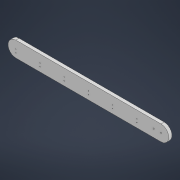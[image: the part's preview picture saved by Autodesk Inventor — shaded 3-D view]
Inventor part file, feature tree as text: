
AUTODESK INVENTOR PART (.ipt)
format: ipt  version: 2021 (Build 250183000, 183)  size: 128,000 bytes
history: native  units: mm
features: sketch x5, hole x3, extrude x2, plane x1, mirror x1
ambient origin geometry x8: Origin, YZ Plane, XZ Plane, XY Plane, X Axis, Y Axis, Z Axis, Center Point
bodies: Solid1 (feature_tree)
feature tree (12):
  extrude  "Extrusion1"  Depth=12.0mm
  hole  "Hole1"  [1 undecoded]
  hole  "Hole2"  [1 undecoded]
  hole  "Hole3"  [1 undecoded]
  plane  "Work Plane1"
  mirror  "Mirror1"
  extrude  "Extrusion2"  Depth=5.0mm
  sketch  "Sketch1"  dims[d0=225.0mm d1=12.0mm]
  sketch  "Sketch2"  dims[d2=5.0mm d3=0.0mm]
  sketch  "Sketch3"  dims[d4=1.9mm d5=6.0mm d6=4.0mm d7=2.0mm d8=90.0deg d9=8.0mm d10=20.594885mm]
  sketch  "Sketch4"  dims[d11=1.0mm d12=6.0mm d13=4.0mm d14=2.0mm d15=90.0deg d16=8.0mm d17=20.594885mm d18=7.5mm]
  sketch  "Sketch5"  dims[d20=1.8mm d21=6.0mm d22=4.0mm d23=2.0mm d24=90.0deg d25=8.0mm d26=20.594885mm d27=5.0mm d28=0.0mm d32=3.85mm d33=37.5mm d34=37.5mm d35=37.5mm d36=37.5mm d37=-2.5mm]
note: 3 required parameter values undecoded (feature->parameter linkage not recoverable at this tier; creation-order binding heuristic only, values carry confidence <= 0.55)
